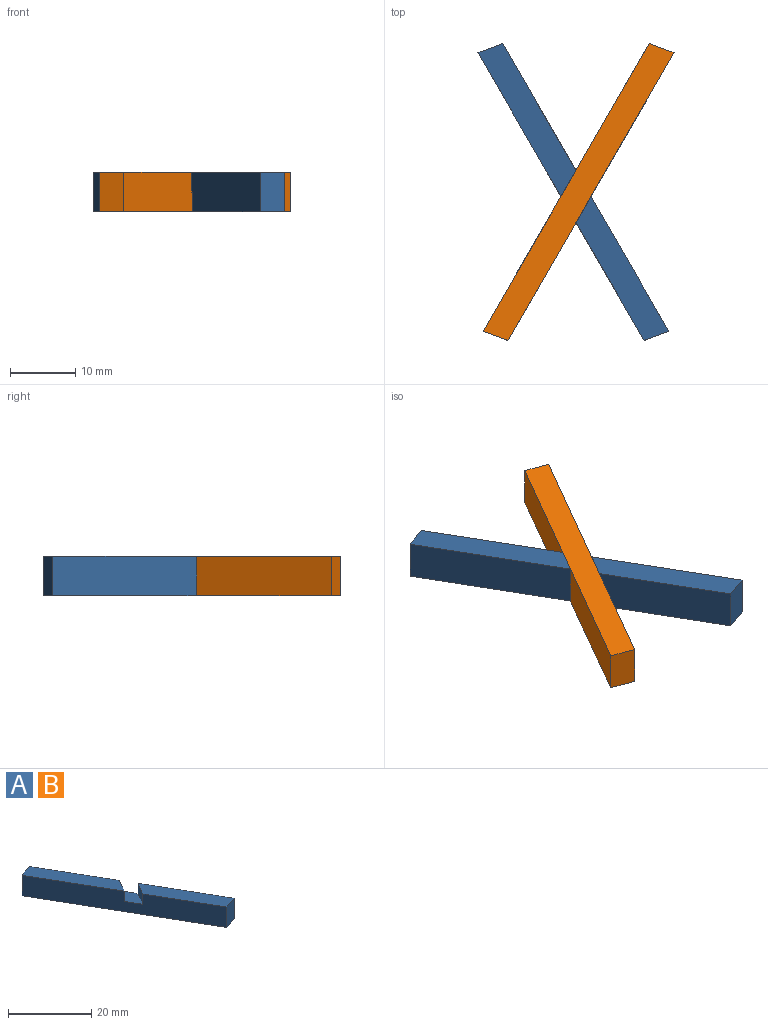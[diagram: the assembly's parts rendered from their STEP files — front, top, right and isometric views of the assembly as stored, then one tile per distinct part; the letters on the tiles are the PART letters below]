
ASSEMBLY  parts=2 mates=1
PART A: 10 faces, bbox 29.3x45.6x6 mm
  f0: plane 44.2x25.52mm, normal (-0.87,-0.5,0), area 292.4mm2, adj f1,f3,f4,f5,f6,f7,f8,f9
  f1: plane 4x3mm, normal (0.87,-0.5,0), area 13.9mm2, adj f0,f2,f4,f6
  f2: plane 44.2x25.52mm, normal (0.87,0.5,0), area 292.4mm2, adj f1,f3,f4,f5,f6,f7,f8,f9
  f3: plane 6x3.82mm, normal (-0.34,0.94,0), area 24.4mm2, adj f0,f2,f4,f5
  f4: plane 23.49x15.07mm, normal (0,0,1), area 96mm2, adj f0,f1,f2,f3
  f5: plane 45.59x29.34mm, normal (0,0,-1), area 204.2mm2, adj f0,f2,f3,f8
  f6: plane 8x4.62mm, normal (0,0,1), area 18.5mm2, adj f0,f1,f2,f7
  f7: plane 4x3mm, normal (-0.87,0.5,0), area 13.9mm2, adj f0,f2,f6,f9
  f8: plane 6x3.82mm, normal (0.34,-0.94,0), area 24.4mm2, adj f0,f2,f5,f9
  f9: plane 22.1x14.27mm, normal (0,0,1), area 89.6mm2, adj f0,f2,f7,f8
PART B: same geometry as A
PLACE A t=(4.78,5.28,-12.13)mm
PLACE B rot(axis=(0,1,0),180deg) t=(9.4,5.28,-6.13)mm
MATE fastened B.f6 <-> A.f6  axis (0,0,-1) through (7.09,5.28,-9.13)mm
